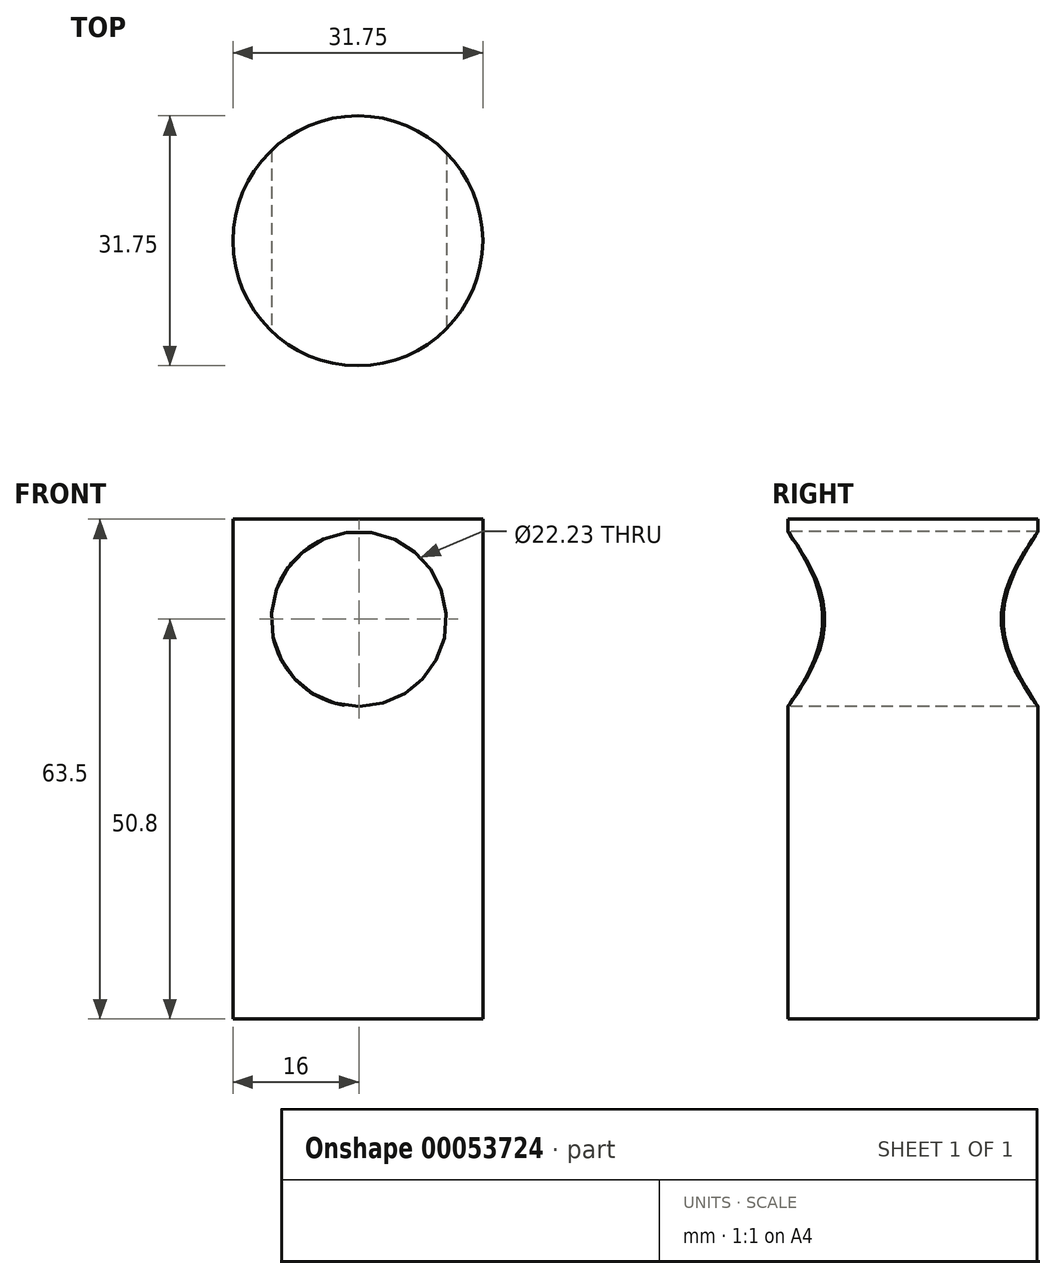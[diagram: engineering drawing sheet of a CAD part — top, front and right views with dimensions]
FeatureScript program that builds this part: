
annotation { "Feature Type Name" : "Feature", "Feature Type Description" : "" }
export const myFeature = defineFeature(function(context is Context, id is Id, definition is map)
    precondition{}
    {
        {
            var Q0;
            Q0=qCreatedBy(makeId("Top.planeOp"),FACE);
            var sketch = newSketch(context, id + "F0", { "sketchPlane" : qUnion([Q0])});
            skCircle(sketch, "E0", {"center": v(-7.75, 13.26) * mm, "radius": 15.88 * mm});
            skSolve(sketch);
        }
        {
            var Q0;
            Q0=makeQuery(id+"F0.imprint","IMPRINT",FACE,{"disambiguationData":[TD([[makeQuery(id+"F0.imprint","IMPRINT",EDGE,{"derivedFrom":sQuery(id+"F0.wireOp",EDGE,"E0")}),1.0]])]});
            extrude(context, id + "F1", {"entities" : qUnion([Q0]), "depth" : 63.5 * mm});
        }
        {
            var Q0;
            Q0=qCreatedBy(makeId("Front.planeOp"),FACE);
            var sketch = newSketch(context, id + "F2", { "sketchPlane" : qUnion([Q0])});
            skCircle(sketch, "E1", {"center": v(-7.62, 50.8) * mm, "radius": 11.11 * mm});
            skSolve(sketch);
        }
        {
            var Q0;
            Q0=makeQuery(id+"F2.imprint","IMPRINT",FACE,{"disambiguationData":[TD([[makeQuery(id+"F2.imprint","IMPRINT",EDGE,{"derivedFrom":sQuery(id+"F2.wireOp",EDGE,"E1")}),1.0]])]});
            var Q1;
            Q1=sQuery(id+"F2.wireOp",EDGE,"E1");
            extrude(context, id + "F3", {"entities" : qUnion([Q0]), "operationType" : NewBodyOperationType.REMOVE, "surfaceEntities" : qUnion([Q1]), "endBound" : BoundingType.SYMMETRIC, "oppositeDirection" : true, "depth" : 76.2 * mm});
        }
    });
